# Revit family: HD49i
name_source: partatom
category: Generic Models
revit_build: Autodesk Revit 2018 (Build: 20190510_1515(x64)
units: mm (PartAtom-declared; Revit-internal decimal feet)

## family parameters
Can host rebar = No
Cut with Voids When Loaded = No
Host = Face
Part Type = Normal
Room Calculation Point = No
Round Connector Dimension = Use Diameter
Shared = No

## types (2) — shared parameters
Cold connection from back of unit = 60 mm
Cold connection from centreline = 27 mm  [stored 0.0885827 ft]
Cold water connection = 20 mm
Cold water inlet = R¾ (20 mm)
Default Elevation = 1219 mm
Efficiency = 82%
Flueing = The internal N49kWi models MUST USE Rinnai flue components—use of non approved flue components will result in a dangerous installation
Gas connection = 20 mm
Gas connection from back of unit = 89 mm
Gas connection from centreline = 89 mm
Gas supply = R¾ (20 mm)
Hot connection from back of unit = 81 mm
Hot connection from centreline = 110 mm  [stored 0.360892 ft]
Hot water capacity = 1.4-37 L/min
Hot water connection = 20 mm
Hot water outlet = R¾ (20 mm)
Ignition system = Direct electronic ignition
Ingress protection rating = IPX2
Input = 11-210 MJ/h
Line pressure maximum = 3.5 kPa (maximum standing pressure under abnormal intermittent conditions is 5.0 kPa).
In the case of commercial metering (i.e. 35-37 kPa coming in), there may be a requirement to regulate the incoming line pressure down
Manufacturer = Rinnai
Minimum water flow = 1.5 L/min
NOx af = 40ppm
Noise level = 54
Nominal operating pressure (water supply) = 200-1000kPa
Nominal water capacity = 28 L/min @25° rise (1680L/h)
Output = 48.8 kW
Power consumption (Normal) = 66 W
Power consumption (antifrost) = 104 W
Power consumption (standby) = 2 W
Type Comments = HD49 units are primarily designed for commercial applications, but can be used for larger hot water capacity residential projects.
Weight = 21 kg

## per-type parameters (varying)
| type | Constraint | Description | Line pressure | Model |
| HD49i (NG) | 1 | HD49 Internal Natural Gas | 1.13-3.0 kPa | HD49iN |
| HD49i (LPG) | 2 | HD49 Internal LPG | 2.75-3.0 kPa | HD49iL |

note: [stored X ft] marks values corroborated as IEEE doubles in the binary element streams (Revit-internal decimal feet)

## geometry (parser evidence)
native form markers: Sweep x2
no freeform markers — native parametric forms only
